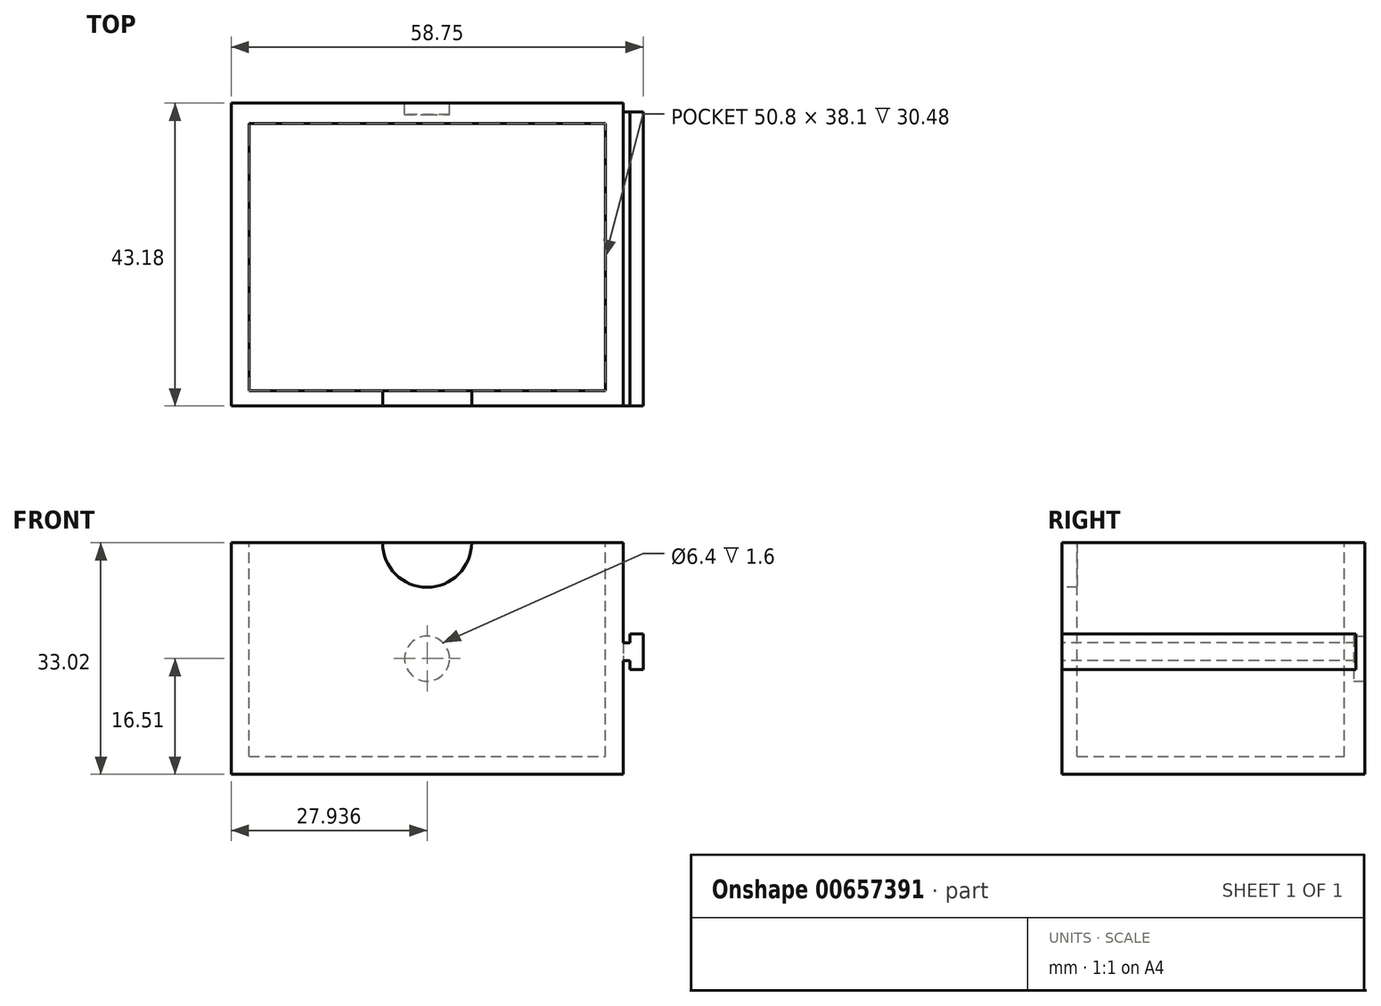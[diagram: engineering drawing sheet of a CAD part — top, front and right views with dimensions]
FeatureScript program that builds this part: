
annotation { "Feature Type Name" : "Feature", "Feature Type Description" : "" }
export const myFeature = defineFeature(function(context is Context, id is Id, definition is map)
    precondition{}
    {
        {
            var Q0;
            Q0=qCreatedBy(makeId("Front.planeOp"),FACE);
            var sketch = newSketch(context, id + "F0", { "sketchPlane" : qUnion([Q0])});
            skLineSegment(sketch, "E0.bottom", {"start": v(-48.42, 33.02) * mm, "end": v(7.46, 33.02) * mm});
            skLineSegment(sketch, "E0.top", {"start": v(-48.42, 0) * mm, "end": v(7.46, 0) * mm});
            skLineSegment(sketch, "E0.left", {"start": v(-48.42, 33.02) * mm, "end": v(-48.42, 0) * mm});
            skLineSegment(sketch, "E0.right", {"start": v(7.46, 33.02) * mm, "end": v(7.46, 0) * mm});
            skSolve(sketch);
        }
        {
            var Q0;
            Q0=qSketchRegion(id+"F0",true);
            extrude(context, id + "F1", {"entities" : qUnion([Q0]), "oppositeDirection" : true, "depth" : 43.18 * mm, "offsetDistance" : 25.4 * mm});
        }
        {
            var Q0;
            Q0=makeQuery(id+"F1.opExtrude","SWEPT_FACE",FACE,{"disambiguationData":[OSD([sQuery(id+"F0.wireOp",EDGE,"E0.bottom")])]});
            var sketch = newSketch(context, id + "F2", { "sketchPlane" : qUnion([Q0])});
            skLineSegment(sketch, "E1.bottom", {"start": v(-45.88, 2.17) * mm, "end": v(4.92, 2.17) * mm});
            skLineSegment(sketch, "E1.top", {"start": v(-45.88, 40.27) * mm, "end": v(4.92, 40.27) * mm});
            skLineSegment(sketch, "E1.left", {"start": v(-45.88, 2.17) * mm, "end": v(-45.88, 40.27) * mm});
            skLineSegment(sketch, "E1.right", {"start": v(4.92, 2.17) * mm, "end": v(4.92, 40.27) * mm});
            skSolve(sketch);
        }
        {
            var Q0;
            Q0=qSketchRegion(id+"F2",true);
            extrude(context, id + "F3", {"entities" : qUnion([Q0]), "operationType" : NewBodyOperationType.REMOVE, "oppositeDirection" : true, "depth" : 30.48 * mm, "offsetDistance" : 25.4 * mm});
        }
        {
            var Q0;
            Q0=makeQuery(id+"F1.opExtrude","CAP_FACE",FACE,{"disambiguationData":[OSD([sQuery(id+"F0.wireOp",EDGE,"E0.bottom"),sQuery(id+"F0.wireOp",EDGE,"E0.top"),sQuery(id+"F0.wireOp",EDGE,"E0.left"),sQuery(id+"F0.wireOp",EDGE,"E0.right")])],"isStart":true});
            var sketch = newSketch(context, id + "F4", { "sketchPlane" : qUnion([Q0])});
            skCircle(sketch, "E2", {"center": v(-20.48, 33.02) * mm, "radius": 6.35 * mm});
            skSolve(sketch);
        }
        {
            var Q0;
            Q0=qSketchRegion(id+"F4",true);
            extrude(context, id + "F5", {"entities" : qUnion([Q0]), "operationType" : NewBodyOperationType.REMOVE, "oppositeDirection" : true, "depth" : 25.4 * mm, "offsetDistance" : 25.4 * mm});
        }
        {
            var Q0;
            Q0=makeQuery(id+"F1.opExtrude","CAP_FACE",FACE,{"disambiguationData":[OSD([sQuery(id+"F0.wireOp",EDGE,"E0.bottom"),sQuery(id+"F0.wireOp",EDGE,"E0.top"),sQuery(id+"F0.wireOp",EDGE,"E0.left"),sQuery(id+"F0.wireOp",EDGE,"E0.right")])],"isStart":false});
            var sketch = newSketch(context, id + "F6", { "sketchPlane" : qUnion([Q0])});
            skCircle(sketch, "E3", {"center": v(20.48, 16.51) * mm, "radius": 3.2 * mm});
            skPoint(sketch, "E3.centerSnap0", {"position": v(-7.46, 16.51) * mm});
            skPoint(sketch, "E3.centerSnap1", {"position": v(20.48, 33.02) * mm});
            skSolve(sketch);
        }
        {
            var Q0;
            Q0=qSketchRegion(id+"F6",true);
            extrude(context, id + "F7", {"entities" : qUnion([Q0]), "operationType" : NewBodyOperationType.REMOVE, "oppositeDirection" : true, "depth" : 1.6 * mm, "offsetDistance" : 25.4 * mm});
        }
        {
            var Q0;
            Q0=makeQuery(id+"F1.opExtrude","CAP_FACE",FACE,{"disambiguationData":[OSD([sQuery(id+"F0.wireOp",EDGE,"E0.bottom"),sQuery(id+"F0.wireOp",EDGE,"E0.top"),sQuery(id+"F0.wireOp",EDGE,"E0.left"),sQuery(id+"F0.wireOp",EDGE,"E0.right")])],"isStart":true});
            var sketch = newSketch(context, id + "F8", { "sketchPlane" : qUnion([Q0])});
            skLineSegment(sketch, "E4.bottom", {"start": v(8.42, 18.75) * mm, "end": v(6.52, 18.75) * mm});
            skLineSegment(sketch, "E4.top", {"start": v(8.42, 16.2) * mm, "end": v(6.52, 16.2) * mm});
            skPoint(sketch, "E4.middle", {"position": v(7.15, 17.48) * mm});
            skLineSegment(sketch, "E5.bottom", {"start": v(10.33, 20.02) * mm, "end": v(8.42, 20.02) * mm});
            skLineSegment(sketch, "E5.top", {"start": v(10.33, 14.94) * mm, "end": v(8.42, 14.94) * mm});
            skLineSegment(sketch, "E5.left", {"start": v(10.33, 20.02) * mm, "end": v(10.33, 14.94) * mm});
            skLineSegment(sketch, "E6", {"start": v(8.42, 18.75) * mm, "end": v(8.42, 20.02) * mm});
            skLineSegment(sketch, "E7", {"start": v(8.42, 16.2) * mm, "end": v(8.42, 14.94) * mm});
            skSolve(sketch);
        }
        {
            var Q0;
            Q0=makeQuery(id+"F8.imprint","IMPRINT",FACE,{"disambiguationData":[TD([[makeQuery(id+"F8.imprint","IMPRINT",EDGE,{"derivedFrom":sQuery(id+"F8.wireOp",EDGE,"E5.bottom")}),1.0]])]});
            extrude(context, id + "F9", {"entities" : qUnion([Q0]), "operationType" : NewBodyOperationType.ADD, "oppositeDirection" : true, "depth" : 41.9 * mm, "offsetDistance" : 25.4 * mm});
        }
    });
